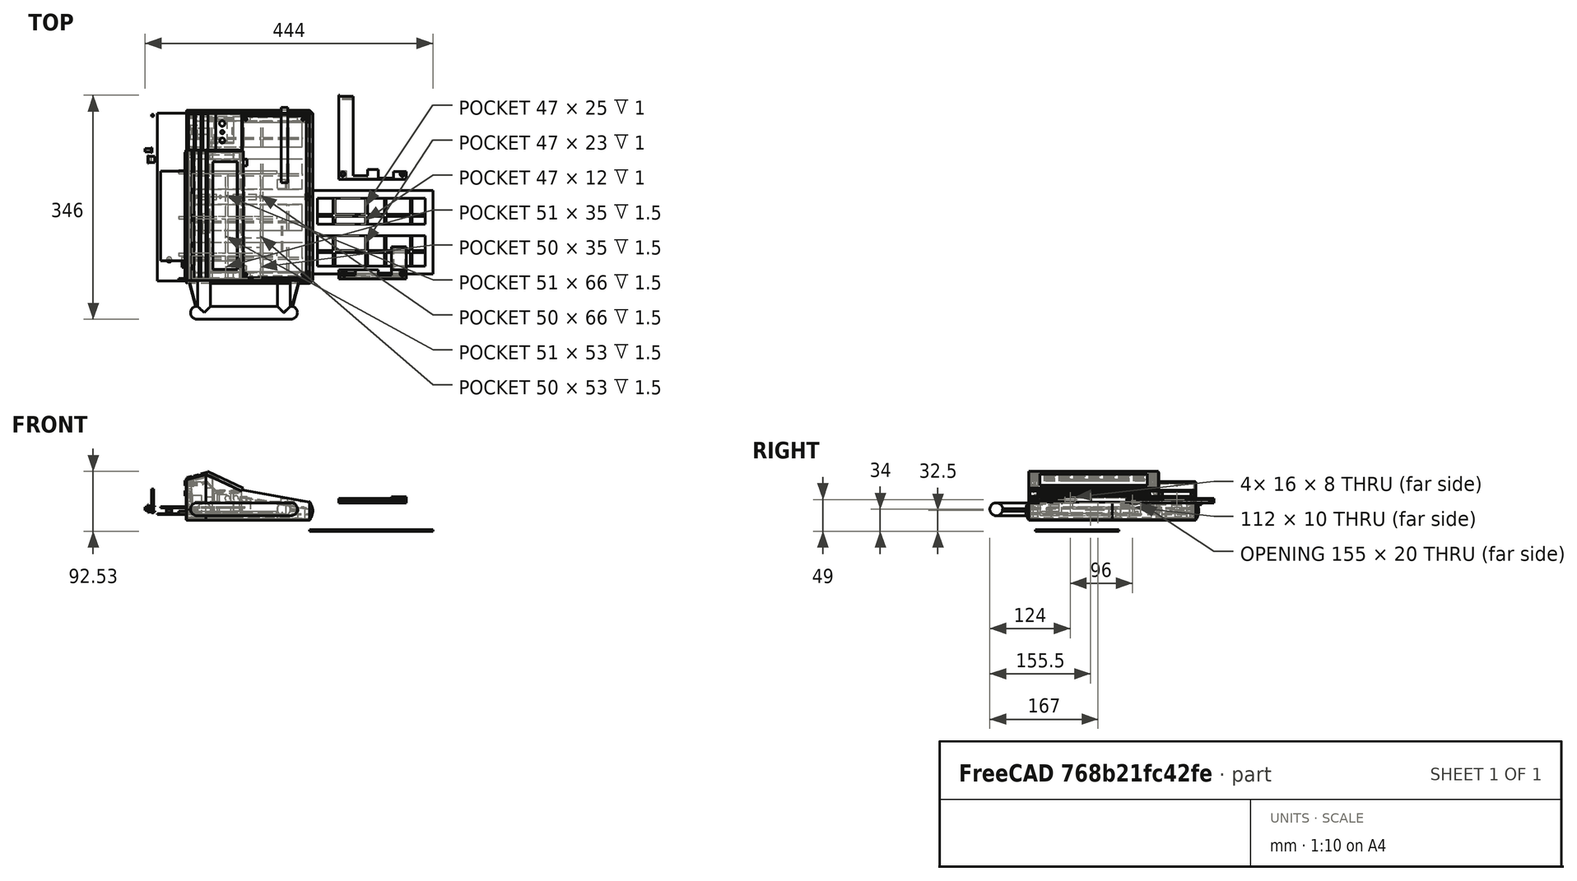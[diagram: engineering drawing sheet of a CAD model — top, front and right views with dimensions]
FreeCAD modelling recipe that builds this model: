
FCSTD DOCUMENT  (FreeCAD 0.20R29603 (Git))
Label: megav4.5
License: All rights reserved
LicenseURL: http://en.wikipedia.org/wiki/All_rights_reserved
objects: Part::Box×241, Part::Cut×105, Part::Cylinder×46, Part::MultiFuse×31, App::DocumentObjectGroup×16, Part::Chamfer×4, Part::Sphere×2, Part::FeaturePython×1
note: 430 computed .brp shape members not serialized (recipe doc carries the construction recipe); baked Part::Feature solids carry a one-line shape summary decoded from their .brp

FEATURE [Part::Box] Box  label="5x50Keyboard"
  AttacherType = Attacher::AttachEngine3D
  Height = 2
  Length = 100
  Width = 250
FEATURE [Part::Box] Box001  label="MainBoardPCB"
  AttacherType = Attacher::AttachEngine3D
  Height = 2
  Length = 130
  Placement = pos=(-125,28,-8) rot=(0,0,1;0rad)
  Width = 138.5
FEATURE [Part::Box] Box002  label="4x40lcd"
  AttacherType = Attacher::AttachEngine3D
  Height = 2
  Length = 54
  Placement = pos=(-56,2,30) rot=(0,1,0;0.296706rad)
  Width = 190
FEATURE [Part::Box] Box050  label="Cube028"
  AttacherType = Attacher::AttachEngine3D
  Height = 9.5
  Length = 11
  Placement = pos=(0,0,35) rot=(0,0,1;0rad)
  Width = 9.5
FEATURE [Part::Box] Box051  label="Cube029"
  AttacherType = Attacher::AttachEngine3D
  Height = 12
  Length = 1
  Placement = pos=(0,-1,34) rot=(0,0,1;0rad)
  Width = 12
FEATURE [Part::Box] Box052  label="Cube030"
  AttacherType = Attacher::AttachEngine3D
  Height = 7.5
  Length = 4.5
  Placement = pos=(5,-1,36) rot=(0,0,1;0rad)
  Width = 13
FEATURE [Part::Box] Box053  label="Cube031"
  AttacherType = Attacher::AttachEngine3D
  Height = 6
  Length = 4.5
  Placement = pos=(9,-1,36.75) rot=(0,0,1;0rad)
  Width = 13
FEATURE [Part::Cylinder] Cylinder008
  Angle = 360
  AttacherType = Attacher::AttachEngine3D
  FirstAngle = 0
  Height = 9
  Placement = pos=(-1,5,40) rot=(0,1,0;1.5708rad)
  Radius = 3
  SecondAngle = 0
FEATURE [Part::MultiFuse] Fusion010
  Shapes = -> [Box050,Box051]
FEATURE [Part::Cut] Cut016
  Base = -> Fusion010
  Tool = -> Cylinder008
FEATURE [Part::Cut] Cut017
  Base = -> Cut016
  Tool = -> Box052
FEATURE [Part::Cut] Cut018
  Base = -> Cut017
  Placement = pos=(-145,180,-49) rot=(0,0,1;0rad)
  Tool = -> Box053
FEATURE [App::DocumentObjectGroup] Group007  label="resetbutton-case"
  Group = -> [Cut018]
FEATURE [Part::Box] Box054  label="Cube002"
  AttacherType = Attacher::AttachEngine3D
  Height = 35
  Length = 2.5
  Placement = pos=(0,0,-19.5) rot=(0,0,1;0rad)
  Width = 195
FEATURE [Part::Box] Box004  label="Cube003"
  AttacherType = Attacher::AttachEngine3D
  Height = 10
  Length = 10
  Placement = pos=(-3,65,-15) rot=(0,0,1;0rad)
  Width = 105
FEATURE [Part::Box] Box021  label="reset"
  AttacherType = Attacher::AttachEngine3D
  Height = 10
  Length = 10
  Placement = pos=(-2,175,0) rot=(0,0,1;0rad)
  Width = 10
FEATURE [Part::Cylinder] Cylinder004  label="pwrjack"
  Angle = 360
  AttacherType = Attacher::AttachEngine3D
  FirstAngle = 0
  Height = 10
  Placement = pos=(-3,17,3) rot=(0,1,0;1.5708rad)
  Radius = 3.5
  SecondAngle = 0
FEATURE [Part::Box] Box055  label="Cube032"
  AttacherType = Attacher::AttachEngine3D
  Height = 5.5
  Length = 1.5
  Placement = pos=(7,1,37) rot=(0,0,1;0rad)
  Width = 8
FEATURE [Part::Cylinder] Cylinder009
  Angle = 360
  AttacherType = Attacher::AttachEngine3D
  FirstAngle = 0
  Height = 10
  Placement = pos=(-2,5,40) rot=(0,1,0;1.5708rad)
  Radius = 2.5
  SecondAngle = 0
FEATURE [Part::MultiFuse] Fusion012
  Placement = pos=(-147,194,-49) rot=(0,0,1;0rad)
  Shapes = -> [Cylinder009,Box055]
FEATURE [App::DocumentObjectGroup] Group008  label="resetbutton"
  Group = -> [Fusion012]
FEATURE [Part::Box] Box056  label="base"
  AttacherType = Attacher::AttachEngine3D
  Height = 1.5
  Length = 235
  Placement = pos=(-25,0,-10) rot=(1,0,0;0rad)
  Width = 259
FEATURE [Part::Box] Box027  label="Cube006"
  AttacherType = Attacher::AttachEngine3D
  Height = 4
  Length = 151
  Placement = pos=(8,0,-9) rot=(0,0,1;0rad)
  Width = 4
FEATURE [Part::Box] Box028  label="Cube007"
  AttacherType = Attacher::AttachEngine3D
  Height = 4
  Length = 151
  Placement = pos=(8,166,-9) rot=(0,0,1;0rad)
  Width = 4
FEATURE [Part::Box] Box029  label="Face003"
  AttacherType = Attacher::AttachEngine3D
  Height = 55
  Length = 2
  Placement = pos=(169.2,0,-11) rot=(0,-1,0;0.261799rad)
  Width = 254
FEATURE [Part::Box] Box036  label="Cube014"
  AttacherType = Attacher::AttachEngine3D
  Height = 2
  Length = 151
  Placement = pos=(8,96,-9) rot=(0,0,1;0rad)
  Width = 4
FEATURE [Part::Box] Box037  label="Cube015"
  AttacherType = Attacher::AttachEngine3D
  Height = 2
  Length = 151
  Placement = pos=(8,39,-9) rot=(0,0,1;0rad)
  Width = 4
FEATURE [Part::Box] Box038  label="Cube016"
  AttacherType = Attacher::AttachEngine3D
  Height = 2
  Length = 170
  Placement = pos=(29,0,-9) rot=(0,0,1;1.5708rad)
  Width = 4
FEATURE [Part::Box] Box039  label="Cube017"
  AttacherType = Attacher::AttachEngine3D
  Height = 2
  Length = 170
  Placement = pos=(84,0,-9) rot=(0,0,1;1.5708rad)
  Width = 4
FEATURE [Part::Box] Box040  label="Cube018"
  AttacherType = Attacher::AttachEngine3D
  Height = 2
  Length = 170
  Placement = pos=(138,0,-9) rot=(0,0,1;1.5708rad)
  Width = 4
FEATURE [Part::Cylinder] Cylinder007
  Angle = 360
  AttacherType = Attacher::AttachEngine3D
  FirstAngle = 0
  Height = 47
  Placement = pos=(167.4,94,-8.1) rot=(1,0,0;1.5708rad)
  Radius = 1
  SecondAngle = 0
FEATURE [Part::MultiFuse] Fusion005
  Shapes = -> [Box027,Box028]
FEATURE [Part::Cut] Cut009
  Base = -> Fusion005
  Tool = -> Box029
FEATURE [Part::MultiFuse] Fusion006
  Placement = pos=(-105,-3,-8) rot=(0,0,1;0rad)
  Refine = true
  Shapes = -> [Cut009,Cylinder007,Box036,Box037,Box038,Box039,Box040,Box056]
FEATURE [App::DocumentObjectGroup] Group009  label="CaseBaseold"
  Group = -> [Fusion006]
FEATURE [Part::FeaturePython] Tube002  label="PCBFoot"  # WARN: FeaturePython — macro-defined, semantics opaque (R4)
  AttacherType = Attacher::AttachEngine3D
  Height = 5
  InnerRadius = 1
  OuterRadius = 4
  Placement = pos=(-112,30,-15) rot=(0,0,1;0rad)
FEATURE [Part::Cylinder] Cylinder010
  Angle = 360
  AttacherType = Attacher::AttachEngine3D
  FirstAngle = 0
  Height = 20
  Placement = pos=(5,5,-2) rot=(0,0,1;0rad)
  Radius = 2
  SecondAngle = 0
FEATURE [Part::Cylinder] Cylinder011
  Angle = 360
  AttacherType = Attacher::AttachEngine3D
  FirstAngle = 0
  Height = 20
  Placement = pos=(5,245,-2) rot=(0,0,1;0rad)
  Radius = 2
  SecondAngle = 0
FEATURE [Part::Cylinder] Cylinder012
  Angle = 360
  AttacherType = Attacher::AttachEngine3D
  FirstAngle = 0
  Height = 20
  Placement = pos=(95,245,-2) rot=(0,0,1;0rad)
  Radius = 2
  SecondAngle = 0
FEATURE [Part::Cylinder] Cylinder013
  Angle = 360
  AttacherType = Attacher::AttachEngine3D
  FirstAngle = 0
  Height = 20
  Placement = pos=(95,5,-2) rot=(0,0,1;0rad)
  Radius = 2
  SecondAngle = 0
FEATURE [Part::Cut] Cut019
  Base = -> Box
  Tool = -> Cylinder010
FEATURE [Part::Cut] Cut020
  Base = -> Cut019
  Tool = -> Cylinder011
FEATURE [Part::Cut] Cut021
  Base = -> Cut020
  Tool = -> Cylinder012
FEATURE [Part::Cut] Cut022
  Base = -> Cut021
  Placement = pos=(0,2,5) rot=(0,0,1;0rad)
  Tool = -> Cylinder013
FEATURE [Part::MultiFuse] Fusion
  Placement = pos=(0,0,3) rot=(0,1,0;0.174533rad)
  Shapes = -> [Box002,Cut022]
FEATURE [App::DocumentObjectGroup] Group  label="PCB"
  Group = -> [Box001,Fusion]
FEATURE [Part::Box] Box057  label="pil1"
  AttacherType = Attacher::AttachEngine3D
  Height = 35
  Length = 105
  Placement = pos=(0,-2,-27) rot=(0,0,1;0rad)
  Width = 14
FEATURE [Part::Box] Box058  label="Cube033"
  AttacherType = Attacher::AttachEngine3D
  Height = 41
  Length = 116
  Placement = pos=(-1,-5,8) rot=(0,1,0;0.174533rad)
  Width = 17
FEATURE [Part::Cut] Cut023  label="leftpailslanted"
  Base = -> Box057
  Placement = pos=(0,-1,0) rot=(0,0,1;0rad)
  Tool = -> Box058
FEATURE [Part::Box] Box059  label="pil002"
  AttacherType = Attacher::AttachEngine3D
  Height = 38
  Length = 105
  Placement = pos=(0,-2,-15) rot=(0,0,1;0rad)
  Width = 2
FEATURE [Part::Box] Box060  label="Cube034"
  AttacherType = Attacher::AttachEngine3D
  Height = 41
  Length = 116
  Placement = pos=(-1,-5,18) rot=(0,1,0;0.174533rad)
  Width = 17
FEATURE [Part::Cut] Cut024  label="leftpailslanted001"
  Base = -> Box059
  Placement = pos=(0,-1,2) rot=(0,0,1;0rad)
  Tool = -> Box060
FEATURE [Part::Box] Box061  label="leftpilstop"
  AttacherType = Attacher::AttachEngine3D
  Height = 6
  Length = 2
  Placement = pos=(103,-3,-15) rot=(0,0,1;0rad)
  Width = 14
FEATURE [Part::Box] Box062  label="leftpilsfillremove"
  AttacherType = Attacher::AttachEngine3D
  Height = 46
  Length = 73
  Placement = pos=(13,4,-23) rot=(0,0,1;0rad)
  Width = 10
FEATURE [Part::MultiFuse] Fusion013
  Shapes = -> [Cut023,Cut024,Box061]
FEATURE [Part::Cut] Cut027  label="LeftPillar"
  Base = -> Fusion013
  Tool = -> Box062
FEATURE [Part::Box] Box069  label="lcdpillar"
  AttacherType = Attacher::AttachEngine3D
  Height = 68
  Length = 55
  Placement = pos=(-55,-3,-25) rot=(0,0,1;0rad)
  Width = 14
FEATURE [Part::Box] Box070  label="lcdpillar001slant"
  AttacherType = Attacher::AttachEngine3D
  Height = 58
  Length = 78
  Placement = pos=(-64,-6,48) rot=(0,1,0;0.436332rad)
  Width = 18
FEATURE [Part::Box] Box071  label="lcdpillar001slant001edge"
  AttacherType = Attacher::AttachEngine3D
  Height = 58
  Length = 78
  Placement = pos=(-64,-1,46) rot=(0,1,0;0.436332rad)
  Width = 18
FEATURE [Part::Cut] Cut029
  Base = -> Box069
  Tool = -> Box070
FEATURE [Part::Cut] Cut030
  Base = -> Cut029
  Tool = -> Box071
FEATURE [Part::Box] Box072  label="lcdstopleft"
  AttacherType = Attacher::AttachEngine3D
  Height = 9
  Length = 3
  Placement = pos=(-3,-3,10) rot=(0,0,1;0rad)
  Width = 14
FEATURE [Part::Box] Box073  label="lcdremove"
  AttacherType = Attacher::AttachEngine3D
  Height = 78
  Length = 32
  Placement = pos=(-45,-1,-23) rot=(0,0,1;0rad)
  Width = 17
FEATURE [Part::MultiFuse] Fusion015
  Shapes = -> [Cut030,Box072]
FEATURE [Part::Cut] Cut031  label="leftlcdpillar"
  Base = -> Fusion015
  Tool = -> Box073
FEATURE [Part::Box] Box080  label="lcdpillar002"
  AttacherType = Attacher::AttachEngine3D
  Height = 70
  Length = 55
  Placement = pos=(-55,-3,-26) rot=(0,0,1;0rad)
  Width = 14
FEATURE [Part::Box] Box081  label="lcdpillar001slant002"
  AttacherType = Attacher::AttachEngine3D
  Height = 58
  Length = 78
  Placement = pos=(-64,-6,48) rot=(0,1,0;0.436332rad)
  Width = 18
FEATURE [Part::Box] Box082  label="lcdpillar001slant001edge002"
  AttacherType = Attacher::AttachEngine3D
  Height = 58
  Length = 78
  Placement = pos=(-64,-10,46) rot=(0,1,0;0.436332rad)
  Width = 18
FEATURE [Part::Box] Box084  label="lcdremove002"
  AttacherType = Attacher::AttachEngine3D
  Height = 63
  Length = 32
  Placement = pos=(-45,-9,-17) rot=(0,0,1;0rad)
  Width = 17
FEATURE [Part::Cut] Cut035
  Base = -> Box080
  Tool = -> Box081
FEATURE [Part::Cut] Cut036
  Base = -> Cut035
  Tool = -> Box082
FEATURE [Part::MultiFuse] Fusion019  label="keyboardlcdleftpillar"
  Placement = pos=(0,1,0) rot=(0,0,1;0rad)
  Shapes = -> [Cut027,Cut031]
FEATURE [Part::Box] Box090  label="extcartslot"
  AttacherType = Attacher::AttachEngine3D
  Height = 77
  Length = 30
  Placement = pos=(-130,-3,-39) rot=(0,0,1;0rad)
  Width = 3
FEATURE [Part::Box] Box091  label="Cube039"
  AttacherType = Attacher::AttachEngine3D
  Height = 41
  Length = 107
  Placement = pos=(-150,-8,16.5) rot=(0,-1,0;0.272271rad)
  Width = 10
FEATURE [Part::Cut] Cut041
  Base = -> Box090
  Placement = pos=(0,0,1.57) rot=(0,0,1;0rad)
  Tool = -> Box091
FEATURE [Part::Box] Box093  label="Cube041"
  AttacherType = Attacher::AttachEngine3D
  Height = 37
  Length = 5
  Placement = pos=(-127.5,0,-20) rot=(0,0,1;0rad)
  Width = 5
FEATURE [Part::MultiFuse] Fusion021  label="LeftExtCartSlot"
  Placement = pos=(45,1,12) rot=(0,0,1;0rad)
  Shapes = -> [Cut041,Box093]
FEATURE [Part::Box] Box094  label="extcartslot001"
  AttacherType = Attacher::AttachEngine3D
  Height = 73
  Length = 30
  Placement = pos=(-85,-3,-27) rot=(0,0,1;0rad)
  Width = 3
FEATURE [Part::Box] Box095  label="Cube042"
  AttacherType = Attacher::AttachEngine3D
  Height = 51
  Length = 107
  Placement = pos=(-150,-8,17.5) rot=(0,-1,0;0.272271rad)
  Width = 10
FEATURE [Part::Box] Box097  label="Cube044"
  AttacherType = Attacher::AttachEngine3D
  Height = 37
  Length = 5
  Placement = pos=(-82.5,-7,-15) rot=(0,0,1;0rad)
  Width = 5
FEATURE [Part::Cut] Cut042
  Base = -> Box094
  Tool = -> Box095
FEATURE [Part::MultiFuse] Fusion022  label="RightExtCartSlot001"
  Placement = pos=(0,209.01,0) rot=(0,0,1;0rad)
  Shapes = -> [Cut042,Box097]
FEATURE [Part::Box] Box098  label="Lid"
  AttacherType = Attacher::AttachEngine3D
  Height = 1.5
  Length = 31
  Placement = pos=(-82,-4,22) rot=(0,1,0;0rad)
  Width = 201
FEATURE [Part::Box] Box099  label="LidRib1"
  AttacherType = Attacher::AttachEngine3D
  Height = 1
  Length = 2
  Placement = pos=(-130,-3,61) rot=(0,-1,0;0rad)
  Width = 199
FEATURE [Part::Box] Box100  label="LidRib002"
  AttacherType = Attacher::AttachEngine3D
  Height = 1
  Length = 2
  Placement = pos=(-120,-3,61) rot=(0,-1,0;0rad)
  Width = 199
FEATURE [Part::Box] Box101  label="LidRib003"
  AttacherType = Attacher::AttachEngine3D
  Height = 1
  Length = 2
  Placement = pos=(-110,-3,61) rot=(0,-1,0;0rad)
  Width = 199
FEATURE [Part::Box] Box102  label="LidRib004"
  AttacherType = Attacher::AttachEngine3D
  Height = 1
  Length = 2
  Placement = pos=(-100,-3,61) rot=(0,-1,0;0rad)
  Width = 199
FEATURE [Part::Box] Box103  label="LidRib005"
  AttacherType = Attacher::AttachEngine3D
  Height = 1
  Length = 2
  Placement = pos=(-90,-3,61) rot=(0,-1,0;0rad)
  Width = 199
FEATURE [Part::Box] Box104  label="LidRib006"
  AttacherType = Attacher::AttachEngine3D
  Height = 1
  Length = 2
  Placement = pos=(-80,-7,61) rot=(0,-1,0;0rad)
  Width = 207
FEATURE [Part::Box] Box105  label="LidRib007"
  AttacherType = Attacher::AttachEngine3D
  Height = 1
  Length = 2
  Placement = pos=(-70,-7,61) rot=(0,-1,0;0rad)
  Width = 211
FEATURE [Part::Box] Box106  label="LidRib008"
  AttacherType = Attacher::AttachEngine3D
  Height = 1
  Length = 2
  Placement = pos=(-60,-4,61) rot=(0,-1,0;0rad)
  Width = 205
FEATURE [Part::Box] Box107  label="Cube045"
  AttacherType = Attacher::AttachEngine3D
  Height = 2
  Length = 28
  Placement = pos=(-79,-1,20) rot=(0,0,1;0rad)
  Width = 2
FEATURE [Part::Box] Box108  label="Cube046"
  AttacherType = Attacher::AttachEngine3D
  Height = 2
  Length = 28
  Placement = pos=(-79,192,20) rot=(0,0,1;0rad)
  Width = 2
FEATURE [Part::Box] Box109  label="Cube047"
  AttacherType = Attacher::AttachEngine3D
  Height = 2
  Length = 2
  Placement = pos=(-80,60,20) rot=(0,0,1;0rad)
  Width = 80
FEATURE [Part::MultiFuse] Fusion023  label="Lid001"
  Placement = pos=(0,0,38) rot=(0,1,0;0rad)
  Shapes = -> [Box098,Box107,Box108,Box109]
FEATURE [Part::Cut] Cut043
  Base = -> Fusion023
  Tool = -> Box099
FEATURE [Part::Cut] Cut044
  Base = -> Cut043
  Tool = -> Box100
FEATURE [Part::Cut] Cut045
  Base = -> Cut044
  Tool = -> Box101
FEATURE [Part::Cut] Cut046
  Base = -> Cut045
  Tool = -> Box102
FEATURE [Part::Cut] Cut047
  Base = -> Cut046
  Tool = -> Box103
FEATURE [Part::Cut] Cut048
  Base = -> Cut047
  Tool = -> Box104
FEATURE [Part::Cut] Cut049
  Base = -> Cut048
  Tool = -> Box105
FEATURE [Part::Cut] Cut050  label="Lid002"
  Base = -> Cut049
  Placement = pos=(10,2,0) rot=(0,-1,0;0.272271rad)
  Tool = -> Box106
FEATURE [Part::Box] Box111  label="Cube049"
  AttacherType = Attacher::AttachEngine3D
  Height = 25
  Length = 14
  Placement = pos=(-76,203,-13) rot=(0,0,1;0rad)
  Width = 10
FEATURE [Part::Cut] Cut052  label="RightExtCartSlotWithHole"
  Base = -> Fusion022
  Placement = pos=(0,-10,0) rot=(0,0,1;0rad)
  Tool = -> Box111
FEATURE [Part::Box] Box112  label="Cube050"
  AttacherType = Attacher::AttachEngine3D
  Height = 2
  Length = 104
  Placement = pos=(150,0,0) rot=(0,0,1;0rad)
  Width = 8
FEATURE [Part::Box] Box113  label="Cube051"
  AttacherType = Attacher::AttachEngine3D
  Height = 5.6
  Length = 104
  Placement = pos=(150,0,0) rot=(0,0,1;0rad)
  Width = 4
FEATURE [Part::Box] Box114  label="Cube052"
  AttacherType = Attacher::AttachEngine3D
  Height = 2
  Length = 104
  Placement = pos=(150,0,3.6) rot=(0,0,1;0rad)
  Width = 8
FEATURE [Part::Box] Box115  label="Cube053"
  AttacherType = Attacher::AttachEngine3D
  Height = 2
  Length = 11
  Placement = pos=(150,4,0) rot=(0,0,1;0rad)
  Width = 10
FEATURE [Part::Cylinder] Cylinder
  Angle = 360
  AttacherType = Attacher::AttachEngine3D
  FirstAngle = 0
  Height = 10
  Placement = pos=(156,9,-3) rot=(0,0,1;0rad)
  Radius = 2.5
  SecondAngle = 0
FEATURE [Part::Box] Box116  label="Cube054"
  AttacherType = Attacher::AttachEngine3D
  Height = 2
  Length = 11
  Placement = pos=(150,4,3.6) rot=(0,0,1;0rad)
  Width = 10
FEATURE [Part::Box] Box117  label="Cube055"
  AttacherType = Attacher::AttachEngine3D
  Height = 2
  Length = 11
  Placement = pos=(243,4,3.6) rot=(0,0,1;0rad)
  Width = 10
FEATURE [Part::Box] Box118  label="Cube056"
  AttacherType = Attacher::AttachEngine3D
  Height = 2
  Length = 11
  Placement = pos=(243,4,0) rot=(0,0,1;0rad)
  Width = 10
FEATURE [Part::Cylinder] Cylinder014
  Angle = 360
  AttacherType = Attacher::AttachEngine3D
  FirstAngle = 0
  Height = 10
  Placement = pos=(248,9,-3) rot=(0,0,1;0rad)
  Radius = 2.5
  SecondAngle = 0
FEATURE [Part::MultiFuse] Fusion024
  Shapes = -> [Box112,Box113,Box114,Box115,Box116,Box117,Box118]
FEATURE [Part::Cut] Cut053
  Base = -> Fusion024
  Tool = -> Cylinder014
FEATURE [Part::Cut] Cut054  label="KeyBoardRiser"
  Base = -> Cut053
  Tool = -> Cylinder
FEATURE [Part::Box] Box083  label="lcdstopleft002"
  AttacherType = Attacher::AttachEngine3D
  Height = 9
  Length = 3
  Placement = pos=(-3,-3,10) rot=(0,0,1;0rad)
  Width = 14
FEATURE [Part::MultiFuse] Fusion017
  Shapes = -> [Cut036,Box083]
FEATURE [Part::Cut] Cut037  label="rightlcdpillar002"
  Base = -> Fusion017
  Placement = pos=(0,188,0) rot=(0,0,1;0rad)
  Tool = -> Box084
FEATURE [Part::Box] Box143  label="NewBasePanel008"
  AttacherType = Attacher::AttachEngine3D
  Height = 2.5
  Length = 190
  Placement = pos=(105,8,-45) rot=(0,0,1;0rad)
  Width = 129
FEATURE [Part::Box] Box144  label="NewBasePanel009"
  AttacherType = Attacher::AttachEngine3D
  Height = 2.5
  Length = 166
  Placement = pos=(117,20,-44) rot=(0,0,1;0rad)
  Width = 105
FEATURE [Part::Box] Box145  label="Cube072"
  AttacherType = Attacher::AttachEngine3D
  Height = 1
  Length = 184
  Placement = pos=(105,41,-43) rot=(0,0,1;0rad)
  Width = 3
FEATURE [Part::Box] Box146  label="Cube073"
  AttacherType = Attacher::AttachEngine3D
  Height = 1
  Length = 184.5
  Placement = pos=(105,97,-43) rot=(0,0,1;0rad)
  Width = 3
FEATURE [Part::Box] Box147  label="Cube074"
  AttacherType = Attacher::AttachEngine3D
  Height = 1
  Length = 3
  Placement = pos=(141,8,-43) rot=(0,0,1;0rad)
  Width = 129
FEATURE [Part::Box] Box148  label="Cube075"
  AttacherType = Attacher::AttachEngine3D
  Height = 1
  Length = 3
  Placement = pos=(191,8,-43) rot=(0,0,1;0rad)
  Width = 129
FEATURE [Part::Cut] Cut059
  Base = -> Box143
  Placement = pos=(0,0,1) rot=(0,0,1;0rad)
  Tool = -> Box144
FEATURE [Part::Box] Box149  label="Cube076"
  AttacherType = Attacher::AttachEngine3D
  Height = 1.5
  Length = 186.5
  Placement = pos=(105,67,-43) rot=(0,0,1;0rad)
  Width = 18
FEATURE [Part::Box] Box206  label="pil005"
  AttacherType = Attacher::AttachEngine3D
  Height = 25
  Length = 105
  Placement = pos=(0,-2,-15) rot=(0,0,1;0rad)
  Width = 14
FEATURE [Part::Box] Box207  label="Cube117"
  AttacherType = Attacher::AttachEngine3D
  Height = 41
  Length = 116
  Placement = pos=(-1,-5,8) rot=(0,1,0;0.174533rad)
  Width = 17
FEATURE [Part::Cut] Cut068  label="rightpailslanted003"
  Base = -> Box206
  Placement = pos=(0,99,0) rot=(0,0,1;0rad)
  Tool = -> Box207
FEATURE [Part::Box] Box208  label="Cube"
  AttacherType = Attacher::AttachEngine3D
  Height = 25
  Length = 120
  Placement = pos=(13,95,-18) rot=(0,0,1;0rad)
  Width = 23
FEATURE [Part::Cut] Cut069  label="keyboardcentrepillar"
  Base = -> Cut068
  Placement = pos=(55,43,-9.7) rot=(0,0,1;0rad)
  Tool = -> Box208
FEATURE [App::DocumentObjectGroup] Group010  label="KeyboardPillars"
  Group = -> [Cut069]
FEATURE [Part::Box] Box209  label="LinkPlate"
  AttacherType = Attacher::AttachEngine3D
  Height = 2
  Length = 30
  Placement = pos=(0,49,0) rot=(0,0,1;0rad)
  Width = 15
FEATURE [Part::Box] Box210  label="Cube118"
  AttacherType = Attacher::AttachEngine3D
  Height = 37
  Length = 130
  Placement = pos=(-40,201,19.5) rot=(0,-1,0;0.785398rad)
  Width = 54
FEATURE [Part::Box] Box211  label="Cube119"
  AttacherType = Attacher::AttachEngine3D
  Height = 57
  Length = 85
  Placement = pos=(-85,202,-25) rot=(0,0,1;0rad)
  Width = 2
FEATURE [Part::Box] Box212  label="Cube120"
  AttacherType = Attacher::AttachEngine3D
  Height = 37
  Length = 130
  Placement = pos=(-40,201,19.5) rot=(0,0,1;0rad)
  Width = 54
FEATURE [Part::Cut] Cut070
  Base = -> Box211
  Tool = -> Box210
FEATURE [Part::Cut] Cut071  label="BoxPanel"
  Base = -> Cut070
  Placement = pos=(0,53,0) rot=(0,0,1;0rad)
  Tool = -> Box212
FEATURE [Part::Box] Box213  label="Cube121"
  AttacherType = Attacher::AttachEngine3D
  Height = 27
  Length = 3
  Placement = pos=(-2,252,-22.5) rot=(0,0,1;0rad)
  Width = 2
FEATURE [Part::Box] Box214  label="Cube122"
  AttacherType = Attacher::AttachEngine3D
  Height = 34
  Length = 3
  Placement = pos=(-83,253,-15.5) rot=(0,0,1;0rad)
  Width = 3
FEATURE [Part::Box] Box215  label="BoxPanelSupports"
  AttacherType = Attacher::AttachEngine3D
  Height = 37
  Length = 3
  Placement = pos=(-139,251,-15.5) rot=(0,0,1;0rad)
  Width = 3
FEATURE [Part::MultiFuse] Fusion039  label="BoxPanelRight"
  Placement = pos=(0,-1,0) rot=(0,0,1;0rad)
  Shapes = -> [Cut071,Box214]
FEATURE [Part::Box] Box216  label="Cube123"
  AttacherType = Attacher::AttachEngine3D
  Height = 37
  Length = 83
  Placement = pos=(-83,199,-15.5) rot=(0,0,1;0rad)
  Width = 55
FEATURE [Part::Box] Box217  label="Cube124"
  AttacherType = Attacher::AttachEngine3D
  Height = 36
  Length = 128
  Placement = pos=(-40,199,9.5) rot=(0,-1,0;0.785398rad)
  Width = 58
FEATURE [Part::Box] Box218  label="Cube125"
  AttacherType = Attacher::AttachEngine3D
  Height = 37
  Length = 75
  Placement = pos=(-128,199,-17.5) rot=(0,0,1;0rad)
  Width = 63
FEATURE [Part::Box] Box219  label="Cube126"
  AttacherType = Attacher::AttachEngine3D
  Height = 36
  Length = 128
  Placement = pos=(-118,198,-96.5) rot=(0,-1,0;0.785398rad)
  Width = 60
FEATURE [Part::Cut] Cut072
  Base = -> Box216
  Tool = -> Box217
FEATURE [Part::Cut] Cut073
  Base = -> Cut072
  Tool = -> Box218
FEATURE [Part::Cut] Cut074
  Base = -> Cut073
  Tool = -> Box219
FEATURE [Part::Box] Box220  label="Cube127"
  AttacherType = Attacher::AttachEngine3D
  Height = 37
  Length = 75
  Placement = pos=(-75,199,-29.5) rot=(0,0,1;0rad)
  Width = 63
FEATURE [Part::Box] Box221  label="Cube128"
  AttacherType = Attacher::AttachEngine3D
  Height = 37
  Length = 75
  Placement = pos=(-40,199,9.5) rot=(0,0,1;0rad)
  Width = 63
FEATURE [Part::Cut] Cut075
  Base = -> Cut074
  Tool = -> Box220
FEATURE [Part::Cut] Cut076  label="BoxLidShape"
  Base = -> Cut075
  Tool = -> Box221
FEATURE [Part::Box] Box225  label="BoxPanelSupports004"
  AttacherType = Attacher::AttachEngine3D
  Height = 56
  Length = 8
  Placement = pos=(-60,255,21.5) rot=(1,0,0;1.5708rad)
  Width = 1.5
FEATURE [Part::Box] Box228  label="BoxPanelSupports007"
  AttacherType = Attacher::AttachEngine3D
  Height = 56
  Length = 8
  Placement = pos=(-82,255,21.5) rot=(1,0,0;1.5708rad)
  Width = 1.5
FEATURE [Part::Box] Box229  label="BoxPanelSupports008"
  AttacherType = Attacher::AttachEngine3D
  Height = 56
  Length = 8
  Placement = pos=(-71,255,21.5) rot=(1,0,0;1.5708rad)
  Width = 1.5
FEATURE [Part::MultiFuse] Fusion040  label="BoxLid"
  Placement = pos=(0,0,10) rot=(0,0,1;0rad)
  Shapes = -> [Cut076,Box225,Box228,Box229]
FEATURE [Part::Box] Box232  label="lcdbezelouter"
  AttacherType = Attacher::AttachEngine3D
  Height = 5
  Length = 61
  Placement = pos=(-55,-2,44) rot=(0,1,0;0.436332rad)
  Width = 200
FEATURE [Part::Box] Box233  label="Cube129"
  AttacherType = Attacher::AttachEngine3D
  Height = 10
  Length = 42
  Placement = pos=(-46,15,42) rot=(0,1,0;0.436332rad)
  Width = 166
FEATURE [Part::Cut] Cut077
  Base = -> Box232
  Tool = -> Box233
FEATURE [Part::Box] Box234  label="lcdbezelouter001"
  AttacherType = Attacher::AttachEngine3D
  Height = 5
  Length = 58
  Placement = pos=(-54,0,42) rot=(0,1,0;0.436332rad)
  Width = 196
FEATURE [Part::Cut] Cut078  label="LcdBezel"
  Base = -> Cut077
  Tool = -> Box234
FEATURE [Part::Box] Box235  label="Cube130"
  AttacherType = Attacher::AttachEngine3D
  Height = 2
  Length = 104
  Placement = pos=(150,1,0) rot=(0,0,1;0rad)
  Width = 8
FEATURE [Part::Box] Box236  label="Cube131"
  AttacherType = Attacher::AttachEngine3D
  Height = 5.6
  Length = 104
  Placement = pos=(150,1,0) rot=(0,0,1;0rad)
  Width = 4
FEATURE [Part::Box] Box237  label="Cube132"
  AttacherType = Attacher::AttachEngine3D
  Height = 2
  Length = 104
  Placement = pos=(150,1,3.6) rot=(0,0,1;0rad)
  Width = 8
FEATURE [Part::Box] Box238  label="Cube133"
  AttacherType = Attacher::AttachEngine3D
  Height = 2
  Length = 11
  Placement = pos=(150,4,0) rot=(0,0,1;0rad)
  Width = 10
FEATURE [Part::Box] Box239  label="Cube134"
  AttacherType = Attacher::AttachEngine3D
  Height = 2
  Length = 11
  Placement = pos=(150,4,3.6) rot=(0,0,1;0rad)
  Width = 10
FEATURE [Part::Box] Box240  label="Cube135"
  AttacherType = Attacher::AttachEngine3D
  Height = 2
  Length = 11
  Placement = pos=(243,4,3.6) rot=(0,0,1;0rad)
  Width = 10
FEATURE [Part::Box] Box241  label="Cube136"
  AttacherType = Attacher::AttachEngine3D
  Height = 2
  Length = 11
  Placement = pos=(243,4,0) rot=(0,0,1;0rad)
  Width = 10
FEATURE [Part::Cylinder] Cylinder015
  Angle = 360
  AttacherType = Attacher::AttachEngine3D
  FirstAngle = 0
  Height = 10
  Placement = pos=(156,9,-3) rot=(0,0,1;0rad)
  Radius = 2.5
  SecondAngle = 0
FEATURE [Part::Cylinder] Cylinder016
  Angle = 360
  AttacherType = Attacher::AttachEngine3D
  FirstAngle = 0
  Height = 10
  Placement = pos=(248,9,-3) rot=(0,0,1;0rad)
  Radius = 2.5
  SecondAngle = 0
FEATURE [Part::MultiFuse] Fusion041
  Shapes = -> [Box235,Box236,Box237,Box238,Box239,Box240,Box241]
FEATURE [Part::Cut] Cut079
  Base = -> Fusion041
  Tool = -> Cylinder016
FEATURE [Part::Cut] Cut080  label="KeyBoardRiser001"
  Base = -> Cut079
  Tool = -> Cylinder015
FEATURE [Part::Box] Box243  label="Cube138"
  AttacherType = Attacher::AttachEngine3D
  Height = 7
  Length = 100
  Placement = pos=(150,1,0) rot=(0,0,1;0rad)
  Width = 2
FEATURE [Part::Box] Box244  label="Cube139"
  AttacherType = Attacher::AttachEngine3D
  Height = 2
  Length = 58
  Placement = pos=(150,1,5) rot=(0,0,1;0rad)
  Width = 6
FEATURE [Part::Box] Box246  label="Cube141"
  AttacherType = Attacher::AttachEngine3D
  Height = 7
  Length = 11
  Placement = pos=(150,2,0) rot=(0,0,1;0rad)
  Width = 12
FEATURE [Part::Box] Box247  label="Cube142"
  AttacherType = Attacher::AttachEngine3D
  Height = 7
  Length = 20
  Placement = pos=(234,1,0) rot=(0,0,1;0rad)
  Width = 12
FEATURE [Part::Cylinder] Cylinder017
  Angle = 360
  AttacherType = Attacher::AttachEngine3D
  FirstAngle = 0
  Height = 10
  Placement = pos=(156,9,-3) rot=(0,0,1;0rad)
  Radius = 2.5
  SecondAngle = 0
FEATURE [Part::Cylinder] Cylinder018
  Angle = 360
  AttacherType = Attacher::AttachEngine3D
  FirstAngle = 0
  Height = 10
  Placement = pos=(248,9,-3) rot=(0,0,1;0rad)
  Radius = 2.5
  SecondAngle = 0
FEATURE [Part::Box] Box248  label="Cube143"
  AttacherType = Attacher::AttachEngine3D
  Height = 2
  Length = 22
  Placement = pos=(150,1,5) rot=(0,0,1;0rad)
  Width = 128
FEATURE [Part::Box] Box249  label="Cube144"
  AttacherType = Attacher::AttachEngine3D
  Height = 3
  Length = 17
  Placement = pos=(194,1,4) rot=(0,0,1;0rad)
  Width = 15
FEATURE [Part::Box] Box250  label="Cube145"
  AttacherType = Attacher::AttachEngine3D
  Height = 7
  Length = 1
  Placement = pos=(150,1,0) rot=(0,0,1;0rad)
  Width = 130
FEATURE [Part::Box] Box268  label="Cube163"
  AttacherType = Attacher::AttachEngine3D
  Height = 7
  Length = 101
  Placement = pos=(152,1,0) rot=(0,0,1;0rad)
  Width = 2
FEATURE [Part::Box] Box269  label="Cube164"
  AttacherType = Attacher::AttachEngine3D
  Height = 5
  Length = 101
  Placement = pos=(152,0,2) rot=(0,0,1;0rad)
  Width = 6
FEATURE [Part::Box] Box270  label="Cube165"
  AttacherType = Attacher::AttachEngine3D
  Height = 2
  Length = 24
  Placement = pos=(152,2,0) rot=(0,0,1;0rad)
  Width = 12
FEATURE [Part::Box] Box271  label="Cube166"
  AttacherType = Attacher::AttachEngine3D
  Height = 7
  Length = 11
  Placement = pos=(243,2,0) rot=(0,0,1;0rad)
  Width = 12
FEATURE [Part::Box] Box273  label="Cube168"
  AttacherType = Attacher::AttachEngine3D
  Height = 2
  Length = 36
  Placement = pos=(175,2,5) rot=(0,0,1;0rad)
  Width = 12
FEATURE [Part::Box] Box274  label="Cube169"
  AttacherType = Attacher::AttachEngine3D
  Height = 7
  Length = 1
  Placement = pos=(253,1,0) rot=(0,0,1;0rad)
  Width = 49
FEATURE [Part::Cylinder] Cylinder029
  Angle = 360
  AttacherType = Attacher::AttachEngine3D
  FirstAngle = 0
  Height = 10
  Placement = pos=(158,8,-3) rot=(0,0,1;0rad)
  Radius = 2.5
  SecondAngle = 0
FEATURE [Part::Cylinder] Cylinder030
  Angle = 360
  AttacherType = Attacher::AttachEngine3D
  FirstAngle = 0
  Height = 10
  Placement = pos=(248,8,-3) rot=(0,0,1;0rad)
  Radius = 2.5
  SecondAngle = 0
FEATURE [Part::Box] Box276  label="Cube171"
  AttacherType = Attacher::AttachEngine3D
  Height = 7
  Length = 2
  Placement = pos=(175,2,0) rot=(0,0,1;0rad)
  Width = 12
FEATURE [Part::Box] Box277  label="Cube172"
  AttacherType = Attacher::AttachEngine3D
  Height = 2
  Length = 22
  Placement = pos=(231,1,5) rot=(0,0,1;0rad)
  Width = 13
FEATURE [Part::Box] Box280  label="Cube175"
  AttacherType = Attacher::AttachEngine3D
  Height = 2
  Length = 23
  Placement = pos=(231,14,5) rot=(0,0,1;0rad)
  Width = 36
FEATURE [Part::Box] Box281  label="Cube176"
  AttacherType = Attacher::AttachEngine3D
  Height = 2
  Length = 23
  Placement = pos=(235,15.5,5) rot=(0,0,1;0rad)
  Width = 33
FEATURE [Part::Cut] Cut089
  Base = -> Box280
  Tool = -> Box281
FEATURE [Part::Box] Box282  label="Cube177"
  AttacherType = Attacher::AttachEngine3D
  Height = 1
  Length = 3
  Placement = pos=(220,8,-43) rot=(0,0,1;0rad)
  Width = 129
FEATURE [Part::Box] Box283  label="Cube178"
  AttacherType = Attacher::AttachEngine3D
  Height = 1
  Length = 3
  Placement = pos=(260,8,-43) rot=(0,0,1;0rad)
  Width = 129
FEATURE [Part::MultiFuse] Fusion029  label="NewBasePanelSection"
  Shapes = -> [Cut059,Box145,Box146,Box147,Box148,Box149,Box282,Box283]
FEATURE [Part::Box] Box284  label="NewBasePanel010"
  AttacherType = Attacher::AttachEngine3D
  Height = 2.5
  Length = 190
  Placement = pos=(105,8,-45) rot=(0,0,1;0rad)
  Width = 129
FEATURE [Part::Box] Box285  label="NewBasePanel011"
  AttacherType = Attacher::AttachEngine3D
  Height = 2.5
  Length = 166
  Placement = pos=(117,20,-44) rot=(0,0,1;0rad)
  Width = 105
FEATURE [Part::Box] Box286  label="Cube179"
  AttacherType = Attacher::AttachEngine3D
  Height = 1
  Length = 184
  Placement = pos=(105,41,-43) rot=(0,0,1;0rad)
  Width = 3
FEATURE [Part::Box] Box287  label="Cube180"
  AttacherType = Attacher::AttachEngine3D
  Height = 1
  Length = 184.5
  Placement = pos=(105,97,-43) rot=(0,0,1;0rad)
  Width = 3
FEATURE [Part::Box] Box288  label="Cube181"
  AttacherType = Attacher::AttachEngine3D
  Height = 1
  Length = 3
  Placement = pos=(141,8,-43) rot=(0,0,1;0rad)
  Width = 129
FEATURE [Part::Box] Box289  label="Cube182"
  AttacherType = Attacher::AttachEngine3D
  Height = 1
  Length = 3
  Placement = pos=(191,8,-43) rot=(0,0,1;0rad)
  Width = 129
FEATURE [Part::Box] Box290  label="Cube183"
  AttacherType = Attacher::AttachEngine3D
  Height = 1.5
  Length = 186.5
  Placement = pos=(105,67,-43) rot=(0,0,1;0rad)
  Width = 18
FEATURE [Part::Box] Box291  label="Cube184"
  AttacherType = Attacher::AttachEngine3D
  Height = 1
  Length = 3
  Placement = pos=(220,8,-43) rot=(0,0,1;0rad)
  Width = 129
FEATURE [Part::Box] Box292  label="Cube185"
  AttacherType = Attacher::AttachEngine3D
  Height = 1
  Length = 3
  Placement = pos=(260,8,-43) rot=(0,0,1;0rad)
  Width = 129
FEATURE [Part::Cut] Cut090
  Base = -> Box284
  Placement = pos=(0,0,1) rot=(0,0,1;0rad)
  Tool = -> Box285
FEATURE [Part::MultiFuse] Fusion046  label="NewBasePanelSection001"
  Placement = pos=(-190,-10,17) rot=(0,0,1;0rad)
  Shapes = -> [Cut090,Box286,Box287,Box288,Box289,Box290,Box291,Box292]
FEATURE [Part::Box] Box293  label="NewBasePanel012"
  AttacherType = Attacher::AttachEngine3D
  Height = 2.5
  Length = 190
  Placement = pos=(105,8,-45) rot=(0,0,1;0rad)
  Width = 129
FEATURE [Part::Box] Box294  label="NewBasePanel013"
  AttacherType = Attacher::AttachEngine3D
  Height = 2.5
  Length = 166
  Placement = pos=(117,20,-44) rot=(0,0,1;0rad)
  Width = 105
FEATURE [Part::Box] Box295  label="Cube186"
  AttacherType = Attacher::AttachEngine3D
  Height = 1
  Length = 184
  Placement = pos=(105,41,-43) rot=(0,0,1;0rad)
  Width = 3
FEATURE [Part::Box] Box296  label="Cube187"
  AttacherType = Attacher::AttachEngine3D
  Height = 1
  Length = 184.5
  Placement = pos=(105,97,-43) rot=(0,0,1;0rad)
  Width = 3
FEATURE [Part::Box] Box297  label="Cube188"
  AttacherType = Attacher::AttachEngine3D
  Height = 1
  Length = 3
  Placement = pos=(141,8,-43) rot=(0,0,1;0rad)
  Width = 129
FEATURE [Part::Box] Box298  label="Cube189"
  AttacherType = Attacher::AttachEngine3D
  Height = 1
  Length = 3
  Placement = pos=(191,8,-43) rot=(0,0,1;0rad)
  Width = 129
FEATURE [Part::Box] Box299  label="Cube190"
  AttacherType = Attacher::AttachEngine3D
  Height = 1.5
  Length = 186.5
  Placement = pos=(105,67,-43) rot=(0,0,1;0rad)
  Width = 18
FEATURE [Part::Box] Box300  label="Cube191"
  AttacherType = Attacher::AttachEngine3D
  Height = 1
  Length = 3
  Placement = pos=(220,8,-43) rot=(0,0,1;0rad)
  Width = 129
FEATURE [Part::Box] Box301  label="Cube192"
  AttacherType = Attacher::AttachEngine3D
  Height = 1
  Length = 3
  Placement = pos=(260,8,-43) rot=(0,0,1;0rad)
  Width = 129
FEATURE [Part::Cut] Cut091
  Base = -> Box293
  Placement = pos=(0,0,1) rot=(0,0,1;0rad)
  Tool = -> Box294
FEATURE [Part::MultiFuse] Fusion047  label="NewBasePanelSection002"
  Placement = pos=(-190,119,17) rot=(0,0,1;0rad)
  Shapes = -> [Cut091,Box295,Box296,Box297,Box298,Box299,Box300,Box301]
FEATURE [Part::Cylinder] Cylinder033
  Angle = 360
  AttacherType = Attacher::AttachEngine3D
  FirstAngle = 0
  Height = 129
  Placement = pos=(87,127,-13) rot=(1,0,0;1.5708rad)
  Radius = 23
  SecondAngle = 0
FEATURE [Part::Box] Box302  label="Cube193"
  AttacherType = Attacher::AttachEngine3D
  Height = 57
  Length = 48
  Placement = pos=(57.5,-10,-43) rot=(0,0,1;0rad)
  Width = 155
FEATURE [Part::Cut] Cut092  label="WristRest1"
  Base = -> Cylinder033
  Placement = pos=(-0.5,0,0.5) rot=(0,0,1;0rad)
  Tool = -> Box302
FEATURE [Part::Cylinder] Cylinder034
  Angle = 360
  AttacherType = Attacher::AttachEngine3D
  FirstAngle = 0
  Height = 129
  Placement = pos=(104.5,127,-24) rot=(1,0,0;1.5708rad)
  Radius = 1.5
  SecondAngle = 0
FEATURE [Part::Box] Box303  label="Cube194"
  AttacherType = Attacher::AttachEngine3D
  Height = 57
  Length = 48
  Placement = pos=(57.5,-10,-43) rot=(0,0,1;0rad)
  Width = 155
FEATURE [Part::Cylinder] Cylinder035
  Angle = 360
  AttacherType = Attacher::AttachEngine3D
  FirstAngle = 0
  Height = 129
  Placement = pos=(87,127,-13) rot=(1,0,0;1.5708rad)
  Radius = 23
  SecondAngle = 0
FEATURE [Part::Cut] Cut093  label="WristRest002"
  Base = -> Cylinder035
  Placement = pos=(-0.5,129,0.5) rot=(0,0,1;0rad)
  Tool = -> Box303
FEATURE [Part::Cylinder] Cylinder036
  Angle = 360
  AttacherType = Attacher::AttachEngine3D
  FirstAngle = 0
  Height = 129
  Placement = pos=(104.5,256,-24) rot=(1,0,0;1.5708rad)
  Radius = 1.5
  SecondAngle = 0
FEATURE [Part::Box] Box304  label="pil006"
  AttacherType = Attacher::AttachEngine3D
  Height = 20
  Length = 105
  Placement = pos=(0,-2,-10) rot=(0,0,1;0rad)
  Width = 5
FEATURE [Part::Box] Box305  label="Cube195"
  AttacherType = Attacher::AttachEngine3D
  Height = 41
  Length = 116
  Placement = pos=(-1,-5,8) rot=(0,1,0;0.174533rad)
  Width = 17
FEATURE [Part::Box] Box306  label="Cube196"
  AttacherType = Attacher::AttachEngine3D
  Height = 25
  Length = 120
  Placement = pos=(8,95,-18) rot=(0,0,1;0rad)
  Width = 23
FEATURE [Part::Cut] Cut094  label="rightpailslanted004"
  Base = -> Box304
  Placement = pos=(0,99,0) rot=(0,0,1;0rad)
  Tool = -> Box305
FEATURE [Part::Cut] Cut095  label="keyboardcentrepillar001"
  Base = -> Cut094
  Placement = pos=(98,25,-16) rot=(0,0,1;0rad)
  Tool = -> Box306
FEATURE [Part::Box] Box307  label="pil007"
  AttacherType = Attacher::AttachEngine3D
  Height = 35
  Length = 105
  Placement = pos=(0,-2,-27) rot=(0,0,1;0rad)
  Width = 14
FEATURE [Part::Box] Box308  label="Cube197"
  AttacherType = Attacher::AttachEngine3D
  Height = 41
  Length = 116
  Placement = pos=(-1,-5,8) rot=(0,1,0;0.174533rad)
  Width = 17
FEATURE [Part::Box] Box309  label="pil008"
  AttacherType = Attacher::AttachEngine3D
  Height = 38
  Length = 105
  Placement = pos=(0,-2,-15) rot=(0,0,1;0rad)
  Width = 2
FEATURE [Part::Box] Box310  label="Cube198"
  AttacherType = Attacher::AttachEngine3D
  Height = 41
  Length = 116
  Placement = pos=(-1,-5,18) rot=(0,1,0;0.174533rad)
  Width = 17
FEATURE [Part::Box] Box311  label="leftpilstop001"
  AttacherType = Attacher::AttachEngine3D
  Height = 6
  Length = 2
  Placement = pos=(103,-3,-15) rot=(0,0,1;0rad)
  Width = 14
FEATURE [Part::Box] Box312  label="leftpilsfillremove001"
  AttacherType = Attacher::AttachEngine3D
  Height = 46
  Length = 73
  Placement = pos=(13,-6,-23) rot=(0,0,1;0rad)
  Width = 10
FEATURE [Part::Cut] Cut096  label="leftpailslanted002"
  Base = -> Box307
  Placement = pos=(0,-1,0) rot=(0,0,1;0rad)
  Tool = -> Box308
FEATURE [Part::Cut] Cut097  label="leftpailslanted003"
  Base = -> Box309
  Placement = pos=(0,11,2) rot=(0,0,1;0rad)
  Tool = -> Box310
FEATURE [Part::MultiFuse] Fusion048
  Shapes = -> [Cut096,Cut097,Box311]
FEATURE [Part::Cut] Cut098  label="RightPillar001"
  Base = -> Fusion048
  Placement = pos=(0,245,0) rot=(0,0,1;0rad)
  Tool = -> Box312
FEATURE [Part::Box] Box313  label="pil009"
  AttacherType = Attacher::AttachEngine3D
  Height = 20
  Length = 105
  Placement = pos=(0,-2,-10) rot=(0,0,1;0rad)
  Width = 5
FEATURE [Part::Box] Box314  label="Cube199"
  AttacherType = Attacher::AttachEngine3D
  Height = 41
  Length = 116
  Placement = pos=(-1,-5,8) rot=(0,1,0;0.174533rad)
  Width = 17
FEATURE [Part::Box] Box315  label="Cube200"
  AttacherType = Attacher::AttachEngine3D
  Height = 25
  Length = 120
  Placement = pos=(8,95,-18) rot=(0,0,1;0rad)
  Width = 23
FEATURE [Part::Cut] Cut099  label="rightpailslanted005"
  Base = -> Box313
  Placement = pos=(0,99,0) rot=(0,0,1;0rad)
  Tool = -> Box314
FEATURE [Part::Cut] Cut100  label="keyboardcentrepillar002"
  Base = -> Cut099
  Placement = pos=(98,30,-16) rot=(0,0,1;0rad)
  Tool = -> Box315
FEATURE [Part::Box] Box320  label="lcdbezelouter002"
  AttacherType = Attacher::AttachEngine3D
  Height = 5
  Length = 61
  Placement = pos=(-55,-2,44) rot=(0,1,0;0.436332rad)
  Width = 200
FEATURE [Part::Box] Box321  label="Cube208"
  AttacherType = Attacher::AttachEngine3D
  Height = 10
  Length = 42
  Placement = pos=(-46,15,42) rot=(0,1,0;0.436332rad)
  Width = 166
FEATURE [Part::Box] Box322  label="lcdbezelouter003"
  AttacherType = Attacher::AttachEngine3D
  Height = 5
  Length = 59
  Placement = pos=(-54,-1,43) rot=(0,1,0;0.436332rad)
  Width = 198
FEATURE [Part::Cut] Cut101
  Base = -> Box320
  Tool = -> Box321
FEATURE [Part::Cut] Cut102  label="LcdBezel001"
  Base = -> Cut101
  Tool = -> Box322
FEATURE [Part::Box] Box323  label="Cube209"
  AttacherType = Attacher::AttachEngine3D
  Height = 2
  Length = 10
  Placement = pos=(0,-2,2.5) rot=(0,0,1;0rad)
  Width = 38
FEATURE [Part::Box] Box324  label="Cube210"
  AttacherType = Attacher::AttachEngine3D
  Height = 2
  Length = 40
  Placement = pos=(0,-1,-6) rot=(0,0,1;0rad)
  Width = 36
FEATURE [Part::Box] Box325  label="Cube211"
  AttacherType = Attacher::AttachEngine3D
  Height = 2.5
  Length = 10
  Placement = pos=(30,-2,2) rot=(0,0,1;0rad)
  Width = 38
FEATURE [Part::Box] Box326  label="Cube212"
  AttacherType = Attacher::AttachEngine3D
  Height = 10.5
  Length = 40
  Placement = pos=(0,-3,-6) rot=(0,0,1;0rad)
  Width = 2
FEATURE [Part::Box] Box327  label="Cube213"
  AttacherType = Attacher::AttachEngine3D
  Height = 10.5
  Length = 40
  Placement = pos=(0,35,-6) rot=(0,0,1;0rad)
  Width = 2
FEATURE [Part::Box] Box328  label="Cube214"
  AttacherType = Attacher::AttachEngine3D
  Height = 8.5
  Length = 2
  Placement = pos=(0,12,-4) rot=(0,0,1;0rad)
  Width = 10
FEATURE [Part::Box] Box329  label="Cube215"
  AttacherType = Attacher::AttachEngine3D
  Height = 2
  Length = 63
  Placement = pos=(2,13,-6) rot=(0,0,1;0rad)
  Width = 10
FEATURE [Part::Box] Box330  label="Cube216"
  AttacherType = Attacher::AttachEngine3D
  Height = 2
  Length = 2
  Placement = pos=(63,13,-5) rot=(0,0,1;0rad)
  Width = 10
FEATURE [Part::MultiFuse] Fusion050  label="batteryholder"
  Placement = pos=(-13,246,-19) rot=(0,0,1;3.14159rad)
  Shapes = -> [Box323,Box324,Box325,Box326,Box327,Box328,Box329,Box330]
FEATURE [Part::Box] Box331  label="lcdbezelouter004"
  AttacherType = Attacher::AttachEngine3D
  Height = 5
  Length = 61
  Placement = pos=(-55,-2,44) rot=(0,1,0;0.436332rad)
  Width = 200
FEATURE [Part::Box] Box332  label="Cube217"
  AttacherType = Attacher::AttachEngine3D
  Height = 10
  Length = 42
  Placement = pos=(-46,15,42) rot=(0,1,0;0.436332rad)
  Width = 166
FEATURE [Part::Box] Box333  label="lcdbezelouter005"
  AttacherType = Attacher::AttachEngine3D
  Height = 5
  Length = 59
  Placement = pos=(-54,-1,43) rot=(0,1,0;0.436332rad)
  Width = 198
FEATURE [Part::Cut] Cut103
  Base = -> Box331
  Tool = -> Box332
FEATURE [Part::Cut] Cut104  label="LcdBezel002"
  Base = -> Cut103
  Tool = -> Box333
FEATURE [App::DocumentObjectGroup] Group015  label="BatteryHolder"
  Group = -> [Fusion050]
FEATURE [Part::Box] Box334  label="Cube218"
  AttacherType = Attacher::AttachEngine3D
  Height = 3
  Length = 85
  Placement = pos=(-83,251,-25) rot=(0,0,1;0rad)
  Width = 3
FEATURE [Part::Box] Box335  label="Cube219"
  AttacherType = Attacher::AttachEngine3D
  Height = 3
  Length = 40
  Placement = pos=(-43,198,15) rot=(0,0,1;0rad)
  Width = 3
FEATURE [Part::Box] Box336  label="Cube220"
  AttacherType = Attacher::AttachEngine3D
  Height = 3
  Length = 23
  Placement = pos=(-83,198,27) rot=(0,0,1;0rad)
  Width = 3
FEATURE [Part::Box] Box337  label="Cube221"
  AttacherType = Attacher::AttachEngine3D
  Height = 34
  Length = 3
  Placement = pos=(-83,198,-15.5) rot=(0,0,1;0rad)
  Width = 3
FEATURE [Part::Box] Box338  label="Cube222"
  AttacherType = Attacher::AttachEngine3D
  Height = 2
  Length = 1
  Placement = pos=(-84,206,-25.5) rot=(0,0,1;0rad)
  Width = 42
FEATURE [Part::Cut] Cut105
  Base = -> Fusion047
  Tool = -> Box338
FEATURE [Part::Cylinder] Cylinder037
  Angle = 360
  AttacherType = Attacher::AttachEngine3D
  FirstAngle = 0
  Height = 2.5
  Placement = pos=(29,127,-27) rot=(0,0,1;0rad)
  Radius = 2
  SecondAngle = 0
FEATURE [Part::Cylinder] Cylinder038
  Angle = 360
  AttacherType = Attacher::AttachEngine3D
  FirstAngle = 0
  Height = 10
  Placement = pos=(-70,127,-29) rot=(0,0,1;0rad)
  Radius = 2
  SecondAngle = 0
FEATURE [Part::Cylinder] Cylinder039
  Angle = 360
  AttacherType = Attacher::AttachEngine3D
  FirstAngle = 0
  Height = 10
  Placement = pos=(-33,127,-29) rot=(0,0,1;0rad)
  Radius = 2
  SecondAngle = 0
FEATURE [Part::Cylinder] Cylinder040
  Angle = 360
  AttacherType = Attacher::AttachEngine3D
  FirstAngle = 0
  Height = 10
  Placement = pos=(29,127,-29) rot=(0,0,1;0rad)
  Radius = 2
  SecondAngle = 0
FEATURE [Part::Cut] Cut106
  Base = -> Cut105
  Tool = -> Cylinder040
FEATURE [Part::Cylinder] Cylinder041
  Angle = 360
  AttacherType = Attacher::AttachEngine3D
  FirstAngle = 0
  Height = 2.5
  Placement = pos=(-33,127,-27) rot=(0,0,1;0rad)
  Radius = 2
  SecondAngle = 0
FEATURE [Part::Cut] Cut107
  Base = -> Fusion046
  Tool = -> Cylinder039
FEATURE [Part::Cylinder] Cylinder042
  Angle = 360
  AttacherType = Attacher::AttachEngine3D
  FirstAngle = 0
  Height = 2.5
  Placement = pos=(-70,127,-27) rot=(0,0,1;0rad)
  Radius = 2
  SecondAngle = 0
FEATURE [Part::Cut] Cut108
  Base = -> Cut107
  Tool = -> Cylinder038
FEATURE [Part::Box] Box339  label="Cube223"
  AttacherType = Attacher::AttachEngine3D
  Height = 2
  Length = 27
  Placement = pos=(-66,127,-25) rot=(0,0,1;0rad)
  Width = 4
FEATURE [Part::Box] Box340  label="Cube224"
  AttacherType = Attacher::AttachEngine3D
  Height = 2
  Length = 36
  Placement = pos=(-13,127,-25) rot=(0,0,1;0rad)
  Width = 4
FEATURE [Part::Box] Box341  label="Cube225"
  AttacherType = Attacher::AttachEngine3D
  Height = 2
  Length = 27
  Placement = pos=(-66,123,-25) rot=(0,0,1;0rad)
  Width = 4
FEATURE [Part::Box] Box342  label="Cube226"
  AttacherType = Attacher::AttachEngine3D
  Height = 2
  Length = 36
  Placement = pos=(-13,123,-25) rot=(0,0,1;0rad)
  Width = 4
FEATURE [Part::Box] Box343  label="Cube227"
  AttacherType = Attacher::AttachEngine3D
  Height = 2
  Length = 2
  Placement = pos=(-82.5,76,-25) rot=(0,0,1;0rad)
  Width = 51
FEATURE [Part::Box] Box344  label="Lid003"
  AttacherType = Attacher::AttachEngine3D
  Height = 1.5
  Length = 31
  Placement = pos=(-86,-2,44) rot=(0,1,0;0rad)
  Width = 201
FEATURE [Part::Box] Box345  label="Cube228"
  AttacherType = Attacher::AttachEngine3D
  Height = 3
  Length = 13
  Placement = pos=(-73,1.1,42) rot=(0,0,1;0rad)
  Width = 2
FEATURE [Part::Box] Box346  label="Cube229"
  AttacherType = Attacher::AttachEngine3D
  Height = 4
  Length = 14
  Placement = pos=(-73,193.8,40) rot=(0,0,1;0rad)
  Width = 2
FEATURE [Part::Box] Box347  label="Cube230"
  AttacherType = Attacher::AttachEngine3D
  Height = 3
  Length = 4
  Placement = pos=(-85.5,24,42) rot=(0,0,1;0rad)
  Width = 153
FEATURE [Part::Box] Box348  label="BoxPanelSupports009"
  AttacherType = Attacher::AttachEngine3D
  Height = 201
  Length = 8
  Placement = pos=(-62,199,45.5) rot=(1,0,0;1.5708rad)
  Width = 1.5
FEATURE [Part::Box] Box349  label="BoxPanelSupports010"
  AttacherType = Attacher::AttachEngine3D
  Height = 201
  Length = 8
  Placement = pos=(-73,199,45.5) rot=(1,0,0;1.5708rad)
  Width = 1.5
FEATURE [Part::Box] Box350  label="BoxPanelSupports011"
  AttacherType = Attacher::AttachEngine3D
  Height = 201
  Length = 8
  Placement = pos=(-84,199,45.5) rot=(1,0,0;1.5708rad)
  Width = 1.5
FEATURE [Part::MultiFuse] Fusion051
  Placement = pos=(9,0,15.3) rot=(0,-1,0;0.261799rad)
  Shapes = -> [Box344,Box345,Box346,Box347,Box348,Box349,Box350]
FEATURE [Part::Box] Box351  label="Cube231"
  AttacherType = Attacher::AttachEngine3D
  Height = 26
  Length = 21
  Placement = pos=(-38,191,-13) rot=(0,0,1;0rad)
  Width = 10
FEATURE [Part::Cut] Cut109
  Base = -> Cut037
  Tool = -> Box351
FEATURE [Part::Box] Box352  label="extcartdupont"
  AttacherType = Attacher::AttachEngine3D
  Height = 20
  Length = 10
  Placement = pos=(-4,15,-15) rot=(0,0,1;0rad)
  Width = 50
FEATURE [Part::Cut] Cut
  Base = -> Box054
  Tool = -> Box004
FEATURE [Part::Cut] Cut110
  Base = -> Cut
  Tool = -> Box352
FEATURE [Part::Box] Box354  label="powerswitch"
  AttacherType = Attacher::AttachEngine3D
  Height = 8
  Length = 16
  Placement = pos=(-92,219,1) rot=(0,1,0;0rad)
  Width = 16
FEATURE [Part::Box] Box355  label="PowerPanelPlate"
  AttacherType = Attacher::AttachEngine3D
  Height = 57
  Length = 2
  Placement = pos=(-85,199.5,-24.5) rot=(0,0,1;0rad)
  Width = 54
FEATURE [Part::Box] Box356  label="usbsocket"
  AttacherType = Attacher::AttachEngine3D
  Height = 3.5
  Length = 16
  Placement = pos=(-92,223,-11) rot=(0,1,0;0rad)
  Width = 8
FEATURE [Part::Box] Box357  label="chargerplate1"
  AttacherType = Attacher::AttachEngine3D
  Height = 2
  Length = 16
  Placement = pos=(-84,216,-14.6) rot=(0,1,0;0rad)
  Width = 22
FEATURE [Part::Box] Box358  label="chargerplate002"
  AttacherType = Attacher::AttachEngine3D
  Height = 2
  Length = 5
  Placement = pos=(-84,216,-11) rot=(0,1,0;0rad)
  Width = 22
FEATURE [Part::Box] Box359  label="Cube233"
  AttacherType = Attacher::AttachEngine3D
  Height = 5
  Length = 5
  Placement = pos=(-84,201.5,10) rot=(0,0,1;0rad)
  Width = 3
FEATURE [Part::Box] Box360  label="Cube234"
  AttacherType = Attacher::AttachEngine3D
  Height = 5
  Length = 5
  Placement = pos=(-84,248.5,10) rot=(0,0,1;0rad)
  Width = 3
FEATURE [Part::Box] Box361  label="Cube235"
  AttacherType = Attacher::AttachEngine3D
  Height = 5
  Length = 3
  Placement = pos=(-79.7,248.5,10) rot=(0,0,1;0rad)
  Width = 5
FEATURE [Part::Box] Box362  label="Cube236"
  AttacherType = Attacher::AttachEngine3D
  Height = 5
  Length = 3
  Placement = pos=(-79.7,199.5,10) rot=(0,0,1;0rad)
  Width = 5
FEATURE [Part::MultiFuse] Fusion052
  Shapes = -> [Box355,Box357,Box358,Box359,Box360,Box361,Box362]
FEATURE [Part::Cut] Cut111
  Base = -> Fusion052
  Tool = -> Box356
FEATURE [Part::Cut] Cut112
  Base = -> Cut111
  Tool = -> Box354
FEATURE [Part::Cylinder] Cylinder044  label="screwhole"
  Angle = 360
  AttacherType = Attacher::AttachEngine3D
  FirstAngle = 0
  Height = 20
  Placement = pos=(-91,227,28) rot=(0,1,0;1.5708rad)
  Radius = 1.5
  SecondAngle = 0
FEATURE [Part::Cut] Cut113
  Base = -> Cut112
  Tool = -> Cylinder044
FEATURE [Part::Box] Box363  label="usbinset"
  AttacherType = Attacher::AttachEngine3D
  Height = 10
  Length = 10
  Placement = pos=(-94,219,-14) rot=(0,0,1;0rad)
  Width = 15.5
FEATURE [Part::Cut] Cut114
  Base = -> Cut113
  Tool = -> Box363
FEATURE [App::DocumentObjectGroup] Group017  label="PowerPanel"
  Group = -> [Cut114]
FEATURE [Part::Cylinder] Cylinder043  label="resetbutton001"
  Angle = 360
  AttacherType = Attacher::AttachEngine3D
  FirstAngle = 0
  Height = 10
  Placement = pos=(-89,182,0) rot=(0,1,0;1.5708rad)
  Radius = 4.2
  SecondAngle = 0
FEATURE [Part::Box] Box364  label="Cube237"
  AttacherType = Attacher::AttachEngine3D
  Height = 7
  Length = 20
  Placement = pos=(150,124,0) rot=(0,0,1;0rad)
  Width = 3
FEATURE [Part::MultiFuse] Fusion042
  Shapes = -> [Box243,Box244,Box246,Box247,Box248,Box249,Box250,Box364]
FEATURE [Part::Cut] Cut081
  Base = -> Fusion042
  Tool = -> Cylinder018
FEATURE [Part::Cut] Cut082  label="KeyboardBezelLeft"
  Base = -> Cut081
  Tool = -> Cylinder017
FEATURE [Part::Cylinder] Cylinder045  label="Cylinder045-screwspace"
  Angle = 360
  AttacherType = Attacher::AttachEngine3D
  FirstAngle = 0
  Height = 5
  Placement = pos=(156,9,2) rot=(0,0,1;0rad)
  Radius = 3.5
  SecondAngle = 0
FEATURE [Part::Cylinder] Cylinder046  label="Cylinder046-screwspace"
  Angle = 360
  AttacherType = Attacher::AttachEngine3D
  FirstAngle = 0
  Height = 5
  Placement = pos=(248,9,2) rot=(0,0,1;0rad)
  Radius = 3.5
  SecondAngle = 0
FEATURE [Part::Cut] Cut116
  Base = -> Cut082
  Tool = -> Cylinder045
FEATURE [Part::Cut] Cut117
  Base = -> Cut116
  Placement = pos=(0,153,0) rot=(0,0,1;0rad)
  Tool = -> Cylinder046
FEATURE [App::DocumentObjectGroup] Group018  label="KeyboardLeftBez"
  Group = -> [Cut117]
FEATURE [Part::Box] Box365  label="Cube238"
  AttacherType = Attacher::AttachEngine3D
  Height = 2
  Length = 23
  Placement = pos=(231,14,7) rot=(0,0,1;0rad)
  Width = 36
FEATURE [Part::Box] Box366  label="Cube239"
  AttacherType = Attacher::AttachEngine3D
  Height = 7
  Length = 12
  Placement = pos=(239,48,0) rot=(0,0,1;0rad)
  Width = 2
FEATURE [Part::MultiFuse] Fusion045
  Shapes = -> [Box268,Box269,Box270,Box271,Box273,Box274,Box276,Box277,Cut089,Box365,Box366]
FEATURE [Part::Cut] Cut085
  Base = -> Fusion045
  Tool = -> Cylinder030
FEATURE [Part::Cut] Cut086  label="KeyboardBezelRight"
  Base = -> Cut085
  Tool = -> Cylinder029
FEATURE [Part::Cylinder] Cylinder047
  Angle = 360
  AttacherType = Attacher::AttachEngine3D
  FirstAngle = 0
  Height = 10
  Placement = pos=(158,8,2) rot=(0,0,1;0rad)
  Radius = 3.5
  SecondAngle = 0
FEATURE [Part::Cylinder] Cylinder048
  Angle = 360
  AttacherType = Attacher::AttachEngine3D
  FirstAngle = 0
  Height = 10
  Placement = pos=(248,8,2) rot=(0,0,1;0rad)
  Radius = 3.5
  SecondAngle = 0
FEATURE [Part::Cut] Cut118
  Base = -> Cut086
  Tool = -> Cylinder047
FEATURE [Part::Cut] Cut119
  Base = -> Cut118
  Tool = -> Cylinder048
FEATURE [Part::Box] Box367  label="Cube240"
  AttacherType = Attacher::AttachEngine3D
  Height = 5
  Length = 23
  Placement = pos=(236,15,0) rot=(0,0,1;0rad)
  Width = 33
FEATURE [Part::Cut] Cut120
  Base = -> Cut119
  Tool = -> Box367
FEATURE [App::DocumentObjectGroup] Group019  label="KeyboardRIghtBez"
  Group = -> [Cut120]
FEATURE [Part::Box] Box368  label="Cube241"
  AttacherType = Attacher::AttachEngine3D
  Height = 26
  Length = 77
  Placement = pos=(-68,180,-25) rot=(1,0,0;0rad)
  Width = 15
FEATURE [Part::Cut] Cut121
  Base = -> Cut109
  Tool = -> Box368
FEATURE [Part::Box] Box369  label="Cube242"
  AttacherType = Attacher::AttachEngine3D
  Height = 48
  Length = 36
  Placement = pos=(-68,180,-25) rot=(1,0,0;0rad)
  Width = 15
FEATURE [Part::Cut] Cut122
  Base = -> Cut121
  Tool = -> Box369
FEATURE [Part::Box] Box370  label="Cube243"
  AttacherType = Attacher::AttachEngine3D
  Height = 14
  Length = 10
  Placement = pos=(-55,185,9) rot=(0,0,1;0rad)
  Width = 10
FEATURE [Part::Box] Box371  label="Cube244"
  AttacherType = Attacher::AttachEngine3D
  Height = 20
  Length = 10
  Placement = pos=(-55,188,2) rot=(1,0,0;0.628319rad)
  Width = 10
FEATURE [Part::Cut] Cut123
  Base = -> Box370
  Tool = -> Box371
FEATURE [Part::Box] Box372  label="Cube245"
  AttacherType = Attacher::AttachEngine3D
  Height = 14
  Length = 10
  Placement = pos=(-55,185,9) rot=(0,0,1;0rad)
  Width = 10
FEATURE [Part::Box] Box373  label="Cube246"
  AttacherType = Attacher::AttachEngine3D
  Height = 20
  Length = 10
  Placement = pos=(-55,188,2) rot=(1,0,0;0.628319rad)
  Width = 10
FEATURE [Part::Cut] Cut124
  Base = -> Box372
  Placement = pos=(42,0,-22) rot=(0,0,1;0rad)
  Tool = -> Box373
FEATURE [Part::Box] Box374  label="Cube247"
  AttacherType = Attacher::AttachEngine3D
  Height = 4
  Length = 71
  Placement = pos=(-78,196,-26) rot=(0,0,1;0rad)
  Width = 5
FEATURE [Part::Box] Box375  label="Cube248"
  AttacherType = Attacher::AttachEngine3D
  Height = 5
  Length = 2
  Placement = pos=(2.5,6,13) rot=(0,0,1;0rad)
  Width = 180
FEATURE [Part::MultiFuse] Fusion011
  Placement = pos=(-86,1,-6.5) rot=(0,0,1;0rad)
  Shapes = -> [Cut110,Box375]
FEATURE [Part::Cut] Cut115
  Base = -> Fusion011
  Tool = -> Cylinder043
FEATURE [Part::Cylinder] Cylinder049  label="nmibutton002"
  Angle = 360
  AttacherType = Attacher::AttachEngine3D
  FirstAngle = 0
  Height = 10
  Placement = pos=(-30,240.3,14) rot=(0,1,0;0rad)
  Radius = 4.2
  SecondAngle = 0
FEATURE [Part::Cylinder] Cylinder050  label="caseled"
  Angle = 360
  AttacherType = Attacher::AttachEngine3D
  FirstAngle = 0
  Height = 10
  Placement = pos=(-30,227,15) rot=(0,1,0;0rad)
  Radius = 2.6
  SecondAngle = 0
FEATURE [Part::Cut] Cut125
  Base = -> Fusion040
  Tool = -> Cylinder049
FEATURE [Part::Cut] Cut126
  Base = -> Cut125
  Tool = -> Cylinder050
FEATURE [Part::Box] Box377  label="esppowerswitch"
  AttacherType = Attacher::AttachEngine3D
  Height = 8
  Length = 16
  Placement = pos=(-94,150,-4) rot=(0,1,0;0rad)
  Width = 16
FEATURE [Part::Cut] Cut127
  Base = -> Cut115
  Placement = pos=(0.5,0,1.5) rot=(0,0,1;0rad)
  Tool = -> Box377
FEATURE [Part::Cylinder] Cylinder051  label="35mmjacksnd"
  Angle = 360
  AttacherType = Attacher::AttachEngine3D
  FirstAngle = 0
  Height = 10
  Placement = pos=(-30,214,15) rot=(1,0,0;0rad)
  Radius = 3.9
  SecondAngle = 0
FEATURE [Part::Cylinder] Cylinder052  label="35mmjack001mic"
  Angle = 360
  AttacherType = Attacher::AttachEngine3D
  FirstAngle = 0
  Height = 10
  Placement = pos=(-9,264.1,7) rot=(1,0,0;1.5708rad)
  Radius = 3.9
  SecondAngle = 0
FEATURE [Part::Cylinder] Cylinder053  label="35mmjack002ear"
  Angle = 360
  AttacherType = Attacher::AttachEngine3D
  FirstAngle = 0
  Height = 10
  Placement = pos=(-22,264.1,7) rot=(1,0,0;1.5708rad)
  Radius = 3.9
  SecondAngle = 0
FEATURE [Part::Cut] Cut128
  Base = -> Cut126
  Tool = -> Cylinder051
FEATURE [Part::Cut] Cut129
  Base = -> Fusion039
  Tool = -> Cylinder052
FEATURE [Part::Cut] Cut130
  Base = -> Cut129
  Tool = -> Cylinder053
FEATURE [Part::Box] Box378  label="Cube250"
  AttacherType = Attacher::AttachEngine3D
  Height = 44
  Length = 8
  Placement = pos=(-42,196,-25) rot=(0,0,1;0rad)
  Width = 8
FEATURE [Part::Cylinder] Cylinder054
  Angle = 360
  AttacherType = Attacher::AttachEngine3D
  FirstAngle = 0
  Height = 51
  Placement = pos=(65,-5,0) rot=(1,0,0;1.5708rad)
  Radius = 10
  SecondAngle = 0
FEATURE [Part::Cylinder] Cylinder055
  Angle = 360
  AttacherType = Attacher::AttachEngine3D
  FirstAngle = 0
  Height = 51
  Placement = pos=(-58,-5,0) rot=(1,0,0;1.5708rad)
  Radius = 10
  SecondAngle = 0
FEATURE [Part::Cylinder] Cylinder056
  Angle = 360
  AttacherType = Attacher::AttachEngine3D
  FirstAngle = 0
  Height = 145
  Placement = pos=(-69,-56,0) rot=(0,1,0;1.5708rad)
  Radius = 10
  SecondAngle = 0
FEATURE [Part::MultiFuse] Fusion054  label="PowerBox1"
  Shapes = -> [Cut128,Cut130]
FEATURE [Part::Box] Box379  label="espuart"
  AttacherType = Attacher::AttachEngine3D
  Height = 15
  Length = 2.5
  Placement = pos=(-85.5,1,-24) rot=(0,1,0;0rad)
  Width = 32
FEATURE [Part::Box] Box380  label="Cube251"
  AttacherType = Attacher::AttachEngine3D
  Height = 9
  Length = 9
  Placement = pos=(-82.5,1,26) rot=(0,0,1;0rad)
  Width = 8
FEATURE [Part::Box] Box381  label="Cube252"
  AttacherType = Attacher::AttachEngine3D
  Height = 9
  Length = 9
  Placement = pos=(-82.5,188,26) rot=(0,0,1;0rad)
  Width = 8
FEATURE [Part::Box] Box382  label="Cube253"
  AttacherType = Attacher::AttachEngine3D
  Height = 10
  Length = 10
  Placement = pos=(-3,48,-10) rot=(0,0,1;0rad)
  Width = 112
FEATURE [Part::Box] Box383  label="Cube254"
  AttacherType = Attacher::AttachEngine3D
  Height = 60
  Length = 2.5
  Placement = pos=(0,0,-19.5) rot=(0,0,1;0rad)
  Width = 195
FEATURE [Part::Box] Box384  label="extcartdupont001"
  AttacherType = Attacher::AttachEngine3D
  Height = 3
  Length = 10
  Placement = pos=(0,9,5) rot=(0,0,1;0rad)
  Width = 31
FEATURE [Part::Box] Box385  label="Cube255"
  AttacherType = Attacher::AttachEngine3D
  Height = 2
  Length = 4
  Placement = pos=(1,7,3) rot=(0,0,1;0rad)
  Width = 35
FEATURE [Part::Box] Box386  label="Cube256"
  AttacherType = Attacher::AttachEngine3D
  Height = 8
  Length = 2
  Placement = pos=(-1.5,0,17) rot=(0,0,1;0rad)
  Width = 195
FEATURE [Part::Box] Box387  label="Cube257"
  AttacherType = Attacher::AttachEngine3D
  Height = 8
  Length = 2
  Placement = pos=(-1.5,0,33) rot=(0,0,1;0rad)
  Width = 195
FEATURE [Part::Box] Box388  label="esppowerswitch001"
  AttacherType = Attacher::AttachEngine3D
  Height = 8
  Length = 16
  Placement = pos=(-92,54,1) rot=(0,1,0;0rad)
  Width = 16
FEATURE [Part::Box] Box389  label="espuart001"
  AttacherType = Attacher::AttachEngine3D
  Height = 3
  Length = 16
  Placement = pos=(-92,18,-16) rot=(0,1,0;0rad)
  Width = 16
FEATURE [Part::Cut] Cut131
  Base = -> Box383
  Tool = -> Box382
FEATURE [Part::Cut] Cut132
  Base = -> Cut131
  Tool = -> Box384
FEATURE [Part::Cylinder] Cylinder057  label="resetbutton002"
  Angle = 360
  AttacherType = Attacher::AttachEngine3D
  FirstAngle = 0
  Height = 10
  Placement = pos=(-86,177,0) rot=(0,1,0;1.5708rad)
  Radius = 4.2
  SecondAngle = 0
FEATURE [Part::MultiFuse] Fusion055
  Placement = pos=(-86,1,-6.5) rot=(0,0,1;0rad)
  Shapes = -> [Cut132,Box385,Box387,Box386]
FEATURE [Part::Cut] Cut133
  Base = -> Fusion055
  Tool = -> Cylinder057
FEATURE [Part::Cut] Cut134
  Base = -> Cut133
  Tool = -> Box388
FEATURE [App::DocumentObjectGroup] Group020  label="Back-Orig"
  Group = -> [Cut134,Box389]
FEATURE [Part::Box] Box390  label="Cube258"
  AttacherType = Attacher::AttachEngine3D
  Height = 26.5
  Length = 2.5
  Placement = pos=(-85,1,10.5) rot=(0,1,0;0rad)
  Width = 195
FEATURE [Part::Box] Box391  label="Cube259"
  AttacherType = Attacher::AttachEngine3D
  Height = 8
  Length = 1.5
  Placement = pos=(-86.5,-2,26.5) rot=(0,0,1;0rad)
  Width = 201
FEATURE [Part::Box] Box392  label="Cube260"
  AttacherType = Attacher::AttachEngine3D
  Height = 8
  Length = 1.5
  Placement = pos=(-86.5,-2,10.5) rot=(0,0,1;0rad)
  Width = 201
FEATURE [Part::Cylinder] Cylinder058
  Angle = 360
  AttacherType = Attacher::AttachEngine3D
  FirstAngle = 0
  Height = 10
  Placement = pos=(-90,192,30) rot=(0,1,0;1.5708rad)
  Radius = 2.5
  SecondAngle = 0
FEATURE [Part::Cylinder] Cylinder059
  Angle = 360
  AttacherType = Attacher::AttachEngine3D
  FirstAngle = 0
  Height = 10
  Placement = pos=(-90,4,30) rot=(0,1,0;1.5708rad)
  Radius = 2.5
  SecondAngle = 0
FEATURE [Part::Cylinder] Cylinder060
  Angle = 360
  AttacherType = Attacher::AttachEngine3D
  FirstAngle = 0
  Height = 200
  Placement = pos=(-94,17,-13) rot=(0,1,0;1.5708rad)
  Radius = 23
  SecondAngle = 0
FEATURE [Part::Box] Box393  label="Cube261"
  AttacherType = Attacher::AttachEngine3D
  Height = 2
  Length = 4
  Placement = pos=(-59.5,71,41.5) rot=(0,0,1;0rad)
  Width = 30
FEATURE [Part::Box] Box394  label="Cube262"
  AttacherType = Attacher::AttachEngine3D
  Height = 2
  Length = 11
  Placement = pos=(-62.5,71,41) rot=(0,0,1;0rad)
  Width = 30
FEATURE [Part::MultiFuse] Fusion056
  Shapes = -> [Box394,Box393,Box391,Box392,Box390]
FEATURE [Part::Cut] Cut135
  Base = -> Fusion056
  Tool = -> Cylinder058
FEATURE [Part::Cut] Cut136
  Base = -> Cut135
  Tool = -> Cylinder059
FEATURE [App::DocumentObjectGroup] Group016  label="NewLid"
  Group = -> [Fusion051,Cut136]
FEATURE [Part::Chamfer] Chamfer
  Base = -> Cylinder060
  Edges = 1 edges r=10: [Edge3]
  Placement = pos=(9,-1,0) rot=(0,0,1;0rad)
FEATURE [Part::Box] Box395  label="Cube263"
  AttacherType = Attacher::AttachEngine3D
  Height = 59
  Length = 250
  Placement = pos=(-97,-2.3,-42) rot=(0,0,1;0rad)
  Width = 54
FEATURE [Part::Cut] Cut137
  Base = -> Chamfer
  Placement = pos=(0,0.4,0.5) rot=(0,0,1;0rad)
  Tool = -> Box395
FEATURE [Part::Box] Box396  label="Cube264"
  AttacherType = Attacher::AttachEngine3D
  Height = 59
  Length = 250
  Placement = pos=(-97,-2.3,-42) rot=(0,0,1;0rad)
  Width = 54
FEATURE [Part::Cylinder] Cylinder061
  Angle = 360
  AttacherType = Attacher::AttachEngine3D
  FirstAngle = 0
  Height = 200
  Placement = pos=(-94,17,-13) rot=(0,1,0;1.5708rad)
  Radius = 23
  SecondAngle = 0
FEATURE [Part::Chamfer] Chamfer001
  Base = -> Cylinder061
  Edges = 1 edges r=10: [Edge3]
  Placement = pos=(9,-1,0) rot=(0,0,1;0rad)
FEATURE [Part::Cut] Cut138
  Base = -> Chamfer001
  Placement = pos=(-0.1,253.4,-25.5) rot=(1,0,0;3.14159rad)
  Tool = -> Box396
FEATURE [App::DocumentObjectGroup] Group011  label="RightSide"
  Group = -> [Cut098,Cut100,Cut052,Cut093,Cylinder036,Box334,Box335,Box336,Box337,Box213,Cut106,Cylinder041,Cylinder042,Box339,Box340,Cut122,Cut123,Cut124,Box374,Box378,Fusion054,Cut138,Box381]
FEATURE [Part::Sphere] Sphere
  Angle1 = -90
  Angle2 = 90
  Angle3 = 360
  AttacherType = Attacher::AttachEngine3D
  Placement = pos=(76,-56,0) rot=(0,0,1;0rad)
  Radius = 10
FEATURE [Part::Sphere] Sphere001
  Angle1 = -90
  Angle2 = 90
  Angle3 = 360
  AttacherType = Attacher::AttachEngine3D
  Placement = pos=(-69,-56,0) rot=(0,0,1;0rad)
  Radius = 10
FEATURE [Part::Box] Box397  label="Cube265"
  AttacherType = Attacher::AttachEngine3D
  Height = 4
  Length = 15
  Placement = pos=(87,-43,0) rot=(0,0,1;0rad)
  Width = 44
FEATURE [Part::Chamfer] Chamfer002
  Base = -> Box397
  Edges = 12 edges r=1.1: [Edge1,Edge2,Edge3,Edge4,Edge5,Edge6,Edge7,Edge8,Edge9,Edge10,Edge11,Edge12]
  Placement = pos=(-10,17,-3) rot=(0,0,-1;0.261799rad)
FEATURE [Part::Box] Box398  label="Cube266"
  AttacherType = Attacher::AttachEngine3D
  Height = 4
  Length = 15
  Placement = pos=(87,-43,0) rot=(0,0,1;0rad)
  Width = 44
FEATURE [Part::Chamfer] Chamfer003
  Base = -> Box398
  Edges = 12 edges r=1.1: [Edge1,Edge2,Edge3,Edge4,Edge5,Edge6,Edge7,Edge8,Edge9,Edge10,Edge11,Edge12]
  Placement = pos=(-165,-33,-3) rot=(0,0,1;0.261799rad)
FEATURE [Part::MultiFuse] Fusion053  label="CarryHandle1"
  Placement = pos=(0,4,-10) rot=(0,0,1;0rad)
  Shapes = -> [Cylinder054,Cylinder055,Cylinder056,Sphere,Sphere001,Chamfer002,Chamfer003]
FEATURE [App::DocumentObjectGroup] Group013  label="LeftSide"
  Group = -> [Cut095,Cylinder034,Cut092,Fusion021,Fusion019,Cylinder037,Cut108,Box342,Box341,Box343,Fusion053,Cut137,Box380]
FEATURE [Part::Box] Box399  label="powerswitch001"
  AttacherType = Attacher::AttachEngine3D
  Height = 8
  Length = 16
  Placement = pos=(-92,219,1) rot=(0,1,0;0rad)
  Width = 16
FEATURE [Part::Box] Box400  label="PowerPanelPlate001"
  AttacherType = Attacher::AttachEngine3D
  Height = 57
  Length = 2
  Placement = pos=(-85,199.7,-24.5) rot=(0,0,1;0rad)
  Width = 53.5
FEATURE [Part::Box] Box401  label="usbsocket001"
  AttacherType = Attacher::AttachEngine3D
  Height = 3.5
  Length = 16
  Placement = pos=(-92,223,-11) rot=(0,1,0;0rad)
  Width = 8
FEATURE [Part::Box] Box402  label="chargerplate003"
  AttacherType = Attacher::AttachEngine3D
  Height = 2
  Length = 16
  Placement = pos=(-84,216,-14.6) rot=(0,1,0;0rad)
  Width = 22
FEATURE [Part::Box] Box403  label="chargerplate004"
  AttacherType = Attacher::AttachEngine3D
  Height = 2
  Length = 5
  Placement = pos=(-84,216,-11) rot=(0,1,0;0rad)
  Width = 22
FEATURE [Part::Box] Box404  label="Cube267"
  AttacherType = Attacher::AttachEngine3D
  Height = 5
  Length = 5
  Placement = pos=(-84,201.5,10) rot=(0,0,1;0rad)
  Width = 3
FEATURE [Part::Box] Box405  label="Cube268"
  AttacherType = Attacher::AttachEngine3D
  Height = 5
  Length = 5
  Placement = pos=(-84,248.5,10) rot=(0,0,1;0rad)
  Width = 3
FEATURE [Part::Box] Box406  label="Cube269"
  AttacherType = Attacher::AttachEngine3D
  Height = 5
  Length = 3
  Placement = pos=(-79,248.5,10) rot=(0,0,1;0rad)
  Width = 5
FEATURE [Part::Box] Box407  label="Cube270"
  AttacherType = Attacher::AttachEngine3D
  Height = 5
  Length = 3
  Placement = pos=(-79,199.5,10) rot=(0,0,1;0rad)
  Width = 5
FEATURE [Part::Box] Box408  label="usbinset001"
  AttacherType = Attacher::AttachEngine3D
  Height = 10
  Length = 10
  Placement = pos=(-94,219,-14) rot=(0,0,1;0rad)
  Width = 15.5
FEATURE [Part::Cylinder] Cylinder062  label="screwhole001"
  Angle = 360
  AttacherType = Attacher::AttachEngine3D
  FirstAngle = 0
  Height = 20
  Placement = pos=(-91,227,28) rot=(0,1,0;1.5708rad)
  Radius = 1.5
  SecondAngle = 0
FEATURE [Part::MultiFuse] Fusion057
  Shapes = -> [Box400,Box402,Box403,Box404,Box405,Box406,Box407]
FEATURE [Part::Cut] Cut139
  Base = -> Fusion057
  Tool = -> Box401
FEATURE [Part::Cut] Cut140
  Base = -> Cut139
  Tool = -> Box399
FEATURE [Part::Cut] Cut141
  Base = -> Cut140
  Tool = -> Cylinder062
FEATURE [Part::Cut] Cut142
  Base = -> Cut141
  Tool = -> Box408
FEATURE [App::DocumentObjectGroup] Group021  label="PowerPanelFuzzy"
  Group = -> [Cut142]
FEATURE [Part::Box] Box409  label="espuart002"
  AttacherType = Attacher::AttachEngine3D
  Height = 16
  Length = 2.5
  Placement = pos=(-85.5,32,-13) rot=(0,1,0;0rad)
  Width = 13
FEATURE [App::DocumentObjectGroup] Group002  label="Back-Bottom"
  Group = -> [Cut127,Box379,Box409]
FEATURE [Part::Box] Box410  label="Cube271"
  AttacherType = Attacher::AttachEngine3D
  Height = 10
  Length = 10
  Placement = pos=(61,149,-3) rot=(0,0,1;0rad)
  Width = 116
FEATURE [Part::Box] Box411  label="pil010"
  AttacherType = Attacher::AttachEngine3D
  Height = 27
  Length = 105
  Placement = pos=(0,-2,-16.2) rot=(0,0,1;0rad)
  Width = 14
FEATURE [Part::Box] Box412  label="Cube272"
  AttacherType = Attacher::AttachEngine3D
  Height = 41
  Length = 116
  Placement = pos=(-1,-5,8) rot=(0,1,0;0.174533rad)
  Width = 17
FEATURE [Part::Box] Box413  label="Cube273"
  AttacherType = Attacher::AttachEngine3D
  Height = 43
  Length = 120
  Placement = pos=(13,92,-31) rot=(0,0,1;0rad)
  Width = 23
FEATURE [Part::Cut] Cut143  label="rightpailslanted006"
  Base = -> Box411
  Placement = pos=(0,99,1) rot=(0,0,1;0rad)
  Tool = -> Box412
FEATURE [Part::Cut] Cut144  label="keyboardcentrepillar003"
  Base = -> Cut143
  Placement = pos=(55,43,-10.8) rot=(0,0,1;0rad)
  Tool = -> Box413
FEATURE [App::DocumentObjectGroup] Group022  label="KeyboardPillars001"
  Group = -> [Cut144]
